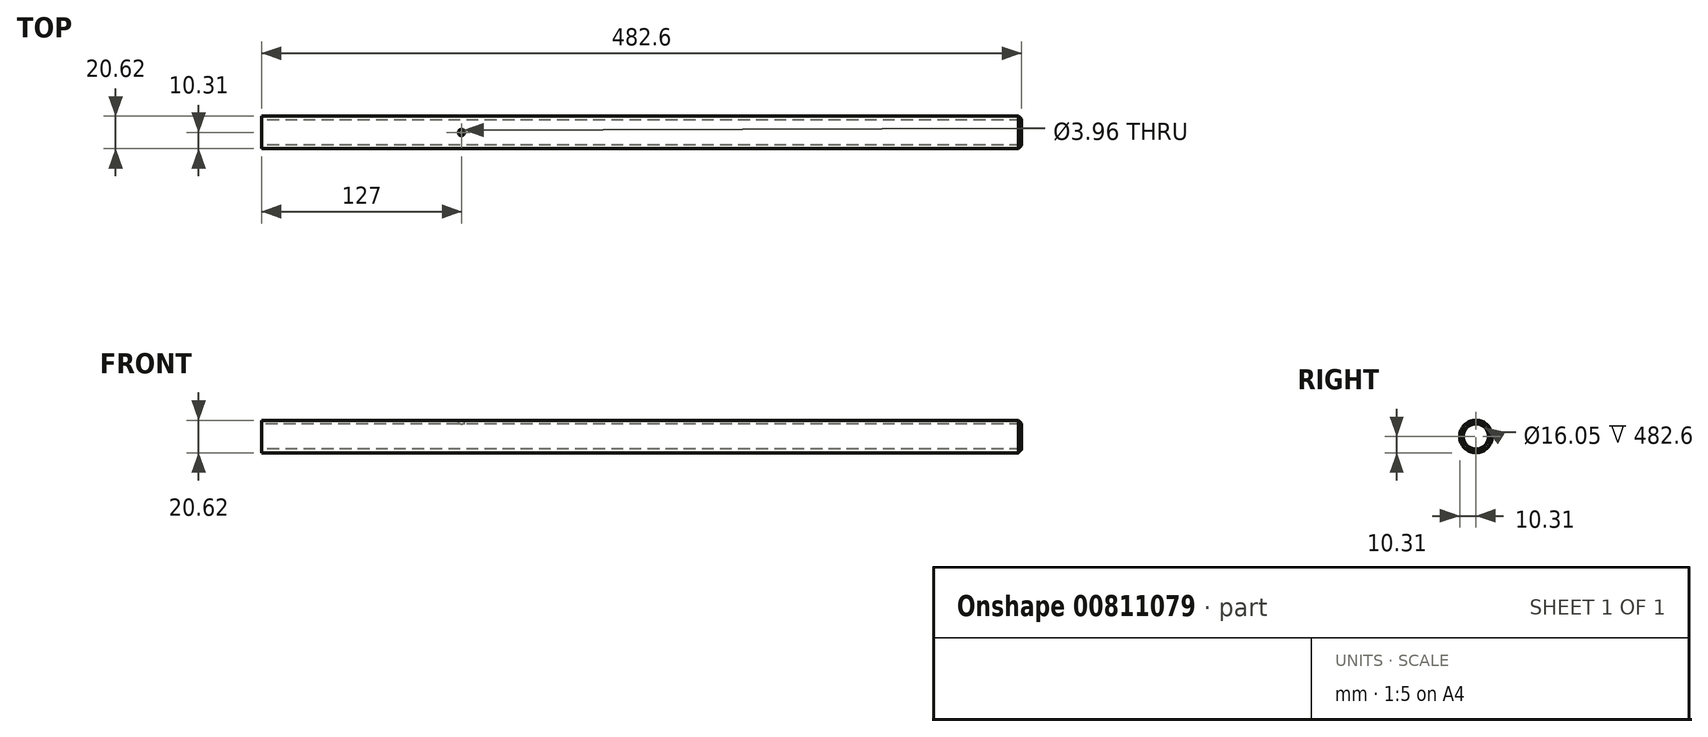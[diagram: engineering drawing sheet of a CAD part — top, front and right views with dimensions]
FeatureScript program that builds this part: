
annotation { "Feature Type Name" : "Feature", "Feature Type Description" : "" }
export const myFeature = defineFeature(function(context is Context, id is Id, definition is map)
    precondition{}
    {
        {
            var Q0;
            Q0=qCreatedBy(makeId("Top.planeOp"),FACE);
            cPlane(context, id + "F0", {"entities" : qUnion([Q0]), "cplaneType" : CPlaneType.OFFSET, "offset" : 10.3 * mm, "width" : 152.4 * mm, "height" : 152.4 * mm});
        }
        {
            var Q0;
            Q0=qCreatedBy(makeId("Right.planeOp"),FACE);
            var sketch = newSketch(context, id + "F1", { "sketchPlane" : qUnion([Q0])});
            skCircle(sketch, "E0", {"center": v(0, 0) * mm, "radius": 10.31 * mm});
            skCircle(sketch, "E1", {"center": v(0, 0) * mm, "radius": 8.03 * mm});
            skSolve(sketch);
        }
        {
            var Q0;
            Q0 = qSketchRegion(id + "F1", true);
            extrude(context, id + "F2", {"entities" : qUnion([Q0]), "depth" : 482.6 * mm, "offsetDistance" : 25.4 * mm, "symmetric" : true});
        }
        {
            var Q0;
            Q0=qCreatedBy(id+"F0.planeOp",FACE);
            var sketch = newSketch(context, id + "F3", { "sketchPlane" : qUnion([Q0])});
            skPoint(sketch, "E2", {"position": v(-114.3, 0) * mm});
            skSolve(sketch);
        }
        {
            var Q0;
            Q0=sQuery(id+"F3.wireOp",VERTEX,"E2");
            var Q1;
            Q1=makeQuery(id+"F2.opExtrude","SWEPT_BODY",BODY,{"disambiguationData":[OSD([sQuery(id+"F1.wireOp",EDGE,"E0"),sQuery(id+"F1.wireOp",EDGE,"E1")])]});
            hole(context, id + "F4", {"style" : HoleStyle.SIMPLE, "endStyle" : HoleEndStyle.BLIND, "holeDiameter" : 3.96 * mm, "majorDiameter" : 6.35 * mm, "holeDepth" : 12.7 * mm, "isTappedThrough" : true, "tappedDepth" : 12.7 * mm, "tapClearance" : 3, "locations" : qUnion([Q0]), "scope" : qUnion([Q1])});
        }
        {
            var Q0;
            Q0=makeQuery(id+"F2.opExtrude","CAP_EDGE",EDGE,{"disambiguationData":[OSD([sQuery(id+"F1.wireOp",EDGE,"E0")])],"isStart":false});
            chamfer(context, id + "F5", {"entities" : qUnion([Q0]), "width" : 1.9 * mm, "tangentPropagation" : true});
        }
    });
